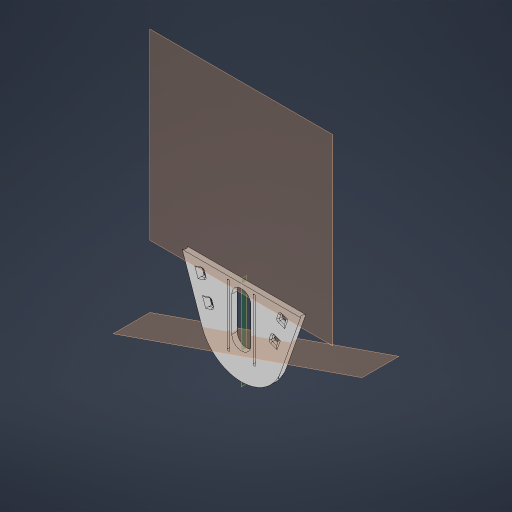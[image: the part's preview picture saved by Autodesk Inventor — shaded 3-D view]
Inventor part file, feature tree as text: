
AUTODESK INVENTOR PART (.ipt)
format: ipt  version: 2024 (Build 280153000, 153)  size: 356,352 bytes
history: native  units: in
note: dims shown in document units (in); Inventor stores cm internally (conversion verified against a paired STEP export)
features: reference x39, plane x3, other x3, extrude x2, fillet x2, sketch x2, mirror x1
ambient origin geometry x8: Origin, YZ Plane, XZ Plane, XY Plane, X Axis, Y Axis, Z Axis, Center Point
bodies: Solid1 (feature_tree)
feature tree (52):
  plane  "Work Plane1"
  extrude  "Extrusion1"  Depth=0.125in
  fillet  "Fillet1"  [1 undecoded]
  plane  "Work Plane2"
  extrude  "Extrusion2"  Depth=0.0625in
  fillet  "Fillet2"  [1 undecoded]
  plane  "Work Plane3"
  mirror  "Mirror1"
  sketch  "Sketch1"  dims[d0=0.25in d1=0.0in d2=0.125in d3=0.0in d4=0.0in]
  reference  "Reference1"
  reference  "Reference2"
  reference  "Reference3"
  reference  "Reference4"
  reference  "Reference5"
  reference  "Reference6"
  reference  "Reference7"
  reference  "Reference8"
  reference  "Reference9"
  reference  "Reference10"
  reference  "Reference11"
  reference  "Reference12"
  reference  "Reference13"
  reference  "Reference14"
  reference  "Reference15"
  reference  "Reference16"
  reference  "Reference17"
  reference  "Reference18"
  reference  "Reference19"
  reference  "Reference20"
  reference  "Reference21"
  reference  "Reference22"
  reference  "Reference23"
  reference  "Reference24"
  reference  "Reference25"
  reference  "Reference26"
  reference  "Reference27"
  reference  "Reference28"
  reference  "Reference29"
  reference  "Reference30"
  reference  "Reference31"
  reference  "Reference32"
  reference  "Reference33"
  reference  "Reference34"
  reference  "Reference35"
  reference  "Reference36"
  reference  "Reference37"
  sketch  "Sketch2"  dims[d5=0.125in d6=0.0625in]
  reference  "Reference38"
  reference  "Reference39"
  other  "<userpath>\CodingProjects\C-AAM\CAD\V1\BoardAssembly.iam"
  other  "BoardAssembly.iam"
  other  "Board:1"
note: 2 required parameter values undecoded (feature->parameter linkage not recoverable at this tier; creation-order binding heuristic only, values carry confidence <= 0.55)
